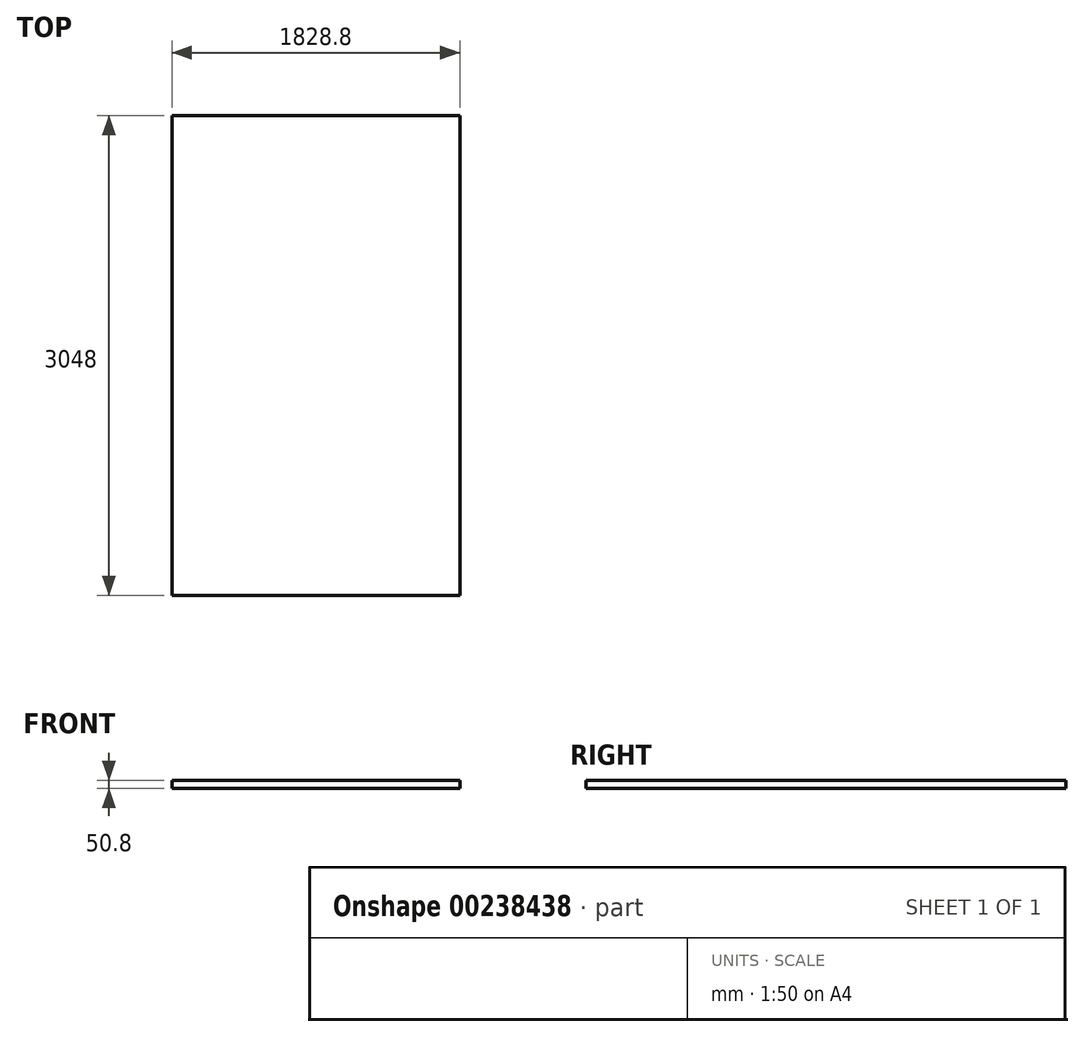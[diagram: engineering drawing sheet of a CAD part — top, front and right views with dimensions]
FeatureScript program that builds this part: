
annotation { "Feature Type Name" : "Feature", "Feature Type Description" : "" }
export const myFeature = defineFeature(function(context is Context, id is Id, definition is map)
    precondition{}
    {
        {
            var Q0;
            Q0=qCreatedBy(makeId("Top.planeOp"),FACE);
            var sketch = newSketch(context, id + "F0", { "sketchPlane" : qUnion([Q0])});
            skLineSegment(sketch, "E0.bottom", {"start": v(-906.74, 1643.35) * mm, "end": v(922.06, 1643.35) * mm});
            skLineSegment(sketch, "E0.top", {"start": v(-906.74, -1404.65) * mm, "end": v(922.06, -1404.65) * mm});
            skLineSegment(sketch, "E0.left", {"start": v(-906.74, 1643.35) * mm, "end": v(-906.74, -1404.65) * mm});
            skLineSegment(sketch, "E0.right", {"start": v(922.06, 1643.35) * mm, "end": v(922.06, -1404.65) * mm});
            skSolve(sketch);
        }
        {
            var Q0;
            Q0=makeQuery(id+"F0.imprint","IMPRINT",FACE,{"disambiguationData":[TD([[makeQuery(id+"F0.imprint","IMPRINT",EDGE,{"derivedFrom":sQuery(id+"F0.wireOp",EDGE,"E0.bottom")}),-1.0]])]});
            extrude(context, id + "F1", {"entities" : qUnion([Q0]), "oppositeDirection" : true, "depth" : 50.8 * mm});
        }
    });
